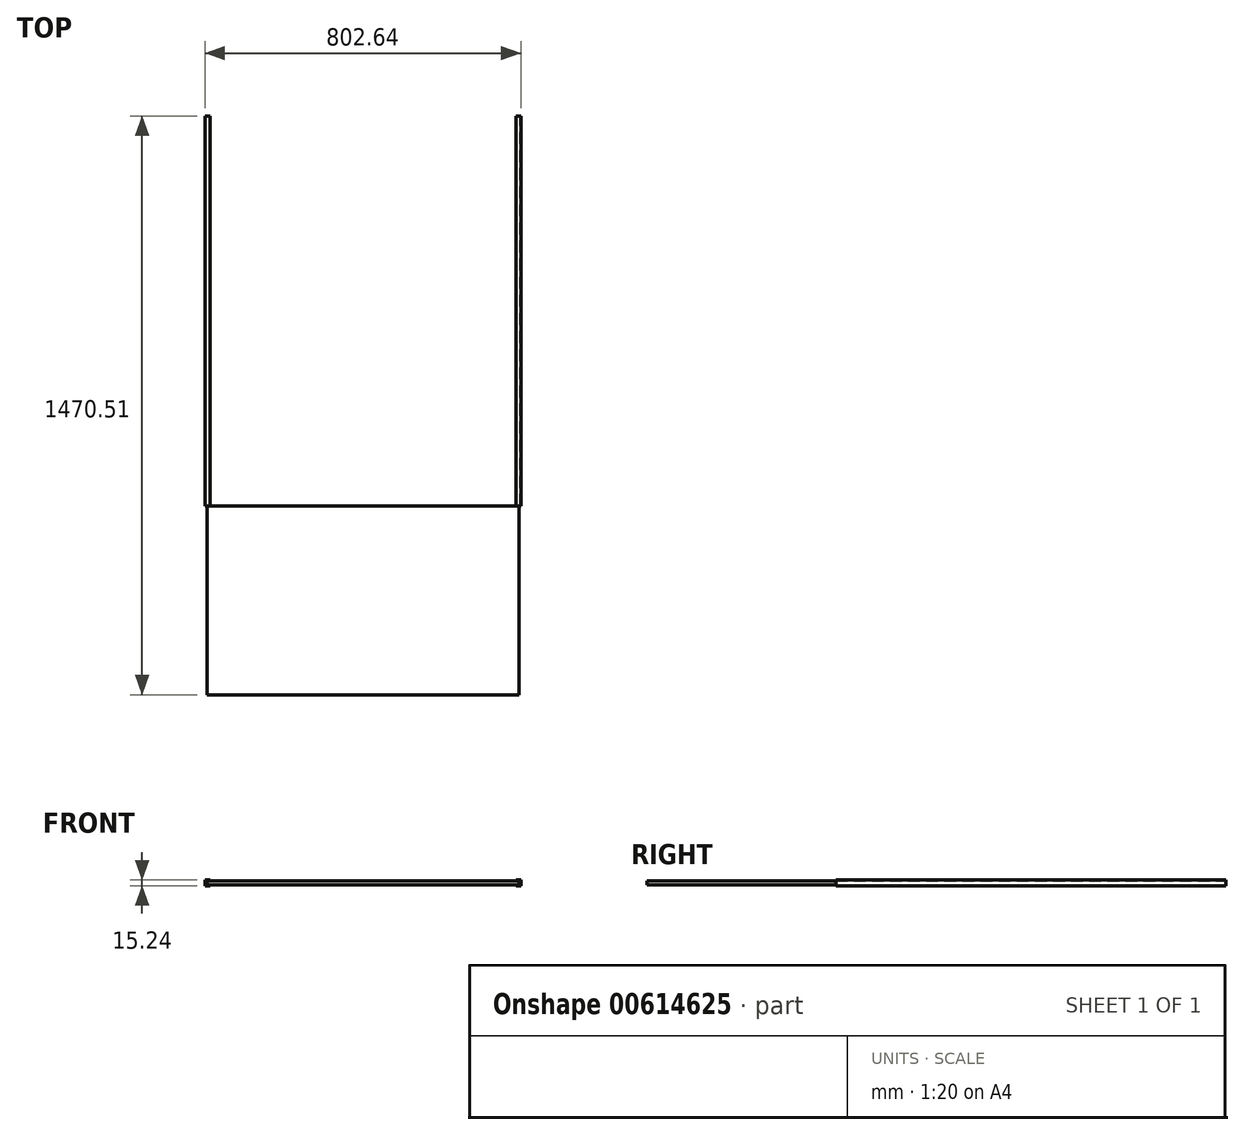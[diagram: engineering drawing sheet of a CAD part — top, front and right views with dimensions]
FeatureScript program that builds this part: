
annotation { "Feature Type Name" : "Feature", "Feature Type Description" : "" }
export const myFeature = defineFeature(function(context is Context, id is Id, definition is map)
    precondition{}
    {
        {
            var Q0;
            Q0=qCreatedBy(makeId("Front.planeOp"),FACE);
            var sketch = newSketch(context, id + "F0", { "sketchPlane" : qUnion([Q0])});
            skLineSegment(sketch, "E0", {"start": v(0, 0) * mm, "end": v(-12.7, 0) * mm});
            skLineSegment(sketch, "E1", {"start": v(-12.7, 0) * mm, "end": v(-12.7, -15.24) * mm});
            skLineSegment(sketch, "E2", {"start": v(-12.7, -15.24) * mm, "end": v(0, -15.24) * mm});
            skLineSegment(sketch, "E3", {"start": v(0, -15.24) * mm, "end": v(0, -12.7) * mm});
            skLineSegment(sketch, "E4", {"start": v(0, -12.7) * mm, "end": v(-10.16, -12.7) * mm});
            skLineSegment(sketch, "E5", {"start": v(-10.16, -12.7) * mm, "end": v(-10.16, -2.54) * mm});
            skLineSegment(sketch, "E6", {"start": v(-10.16, -2.54) * mm, "end": v(0, -2.54) * mm});
            skLineSegment(sketch, "E7", {"start": v(0, -2.54) * mm, "end": v(0, 0) * mm});
            skSolve(sketch);
        }
        {
            var Q0;
            Q0=qSketchRegion(id+"F0",true);
            extrude(context, id + "F1", {"entities" : qUnion([Q0]), "depth" : 990.6 * mm, "offsetDistance" : 25.4 * mm});
        }
        {
            var Q0;
            Q0=makeQuery(id+"F1.opExtrude","CAP_FACE",FACE,{"disambiguationData":[OSD([sQuery(id+"F0.wireOp",EDGE,"E0"),sQuery(id+"F0.wireOp",EDGE,"E1"),sQuery(id+"F0.wireOp",EDGE,"E2"),sQuery(id+"F0.wireOp",EDGE,"E3"),sQuery(id+"F0.wireOp",EDGE,"E4"),sQuery(id+"F0.wireOp",EDGE,"E5"),sQuery(id+"F0.wireOp",EDGE,"E6"),sQuery(id+"F0.wireOp",EDGE,"E7")])],"isStart":false});
            var sketch = newSketch(context, id + "F2", { "sketchPlane" : qUnion([Q0])});
            skLineSegment(sketch, "E8.bottom", {"start": v(-7.62, -2.7) * mm, "end": v(388.62, -2.7) * mm});
            skLineSegment(sketch, "E8.top", {"start": v(-7.62, -12.7) * mm, "end": v(388.62, -12.7) * mm});
            skLineSegment(sketch, "E8.left", {"start": v(-7.62, -2.7) * mm, "end": v(-7.62, -12.7) * mm});
            skLineSegment(sketch, "E8.right", {"start": v(388.62, -2.7) * mm, "end": v(388.62, -12.7) * mm});
            skSolve(sketch);
        }
        {
            var Q0;
            Q0=makeQuery(id+"F2.imprint","IMPRINT",FACE,{"disambiguationData":[TD([[makeQuery(id+"F2.imprint","IMPRINT",EDGE,{"derivedFrom":sQuery(id+"F2.wireOp",EDGE,"E8.bottom")}),-1.0]])]});
            extrude(context, id + "F3", {"entities" : qUnion([Q0]), "depth" : 479.9 * mm, "offsetDistance" : 25.4 * mm});
        }
        {
            var Q0;
            Q0=makeQuery(id+"F3.opExtrude","SWEPT_FACE",FACE,{"disambiguationData":[OSD([sQuery(id+"F2.wireOp",EDGE,"E8.right")])]});
            cPlane(context, id + "F4", {"entities" : qUnion([Q0]), "cplaneType" : CPlaneType.OFFSET, "offset" : 0 * mm, "width" : 152.4 * mm, "height" : 152.4 * mm});
        }
        {
            var Q0;
            Q0=makeQuery(id+"F3.opExtrude","SWEPT_BODY",BODY,{"disambiguationData":[OSD([sQuery(id+"F2.wireOp",EDGE,"E8.bottom"),sQuery(id+"F2.wireOp",EDGE,"E8.top"),sQuery(id+"F2.wireOp",EDGE,"E8.left"),sQuery(id+"F2.wireOp",EDGE,"E8.right")])]});
            var Q1;
            Q1=makeQuery(id+"F1.opExtrude","SWEPT_BODY",BODY,{"disambiguationData":[OSD([sQuery(id+"F0.wireOp",EDGE,"E0"),sQuery(id+"F0.wireOp",EDGE,"E1"),sQuery(id+"F0.wireOp",EDGE,"E2"),sQuery(id+"F0.wireOp",EDGE,"E3"),sQuery(id+"F0.wireOp",EDGE,"E4"),sQuery(id+"F0.wireOp",EDGE,"E5"),sQuery(id+"F0.wireOp",EDGE,"E6"),sQuery(id+"F0.wireOp",EDGE,"E7")])]});
            var Q2;
            Q2=qCreatedBy(id+"F4.planeOp",FACE);
            mirror(context, id + "F5", {"operationType" : NewBodyOperationType.ADD, "entities" : qUnion([Q0, Q1]), "mirrorPlane" : qUnion([Q2])});
        }
    });
